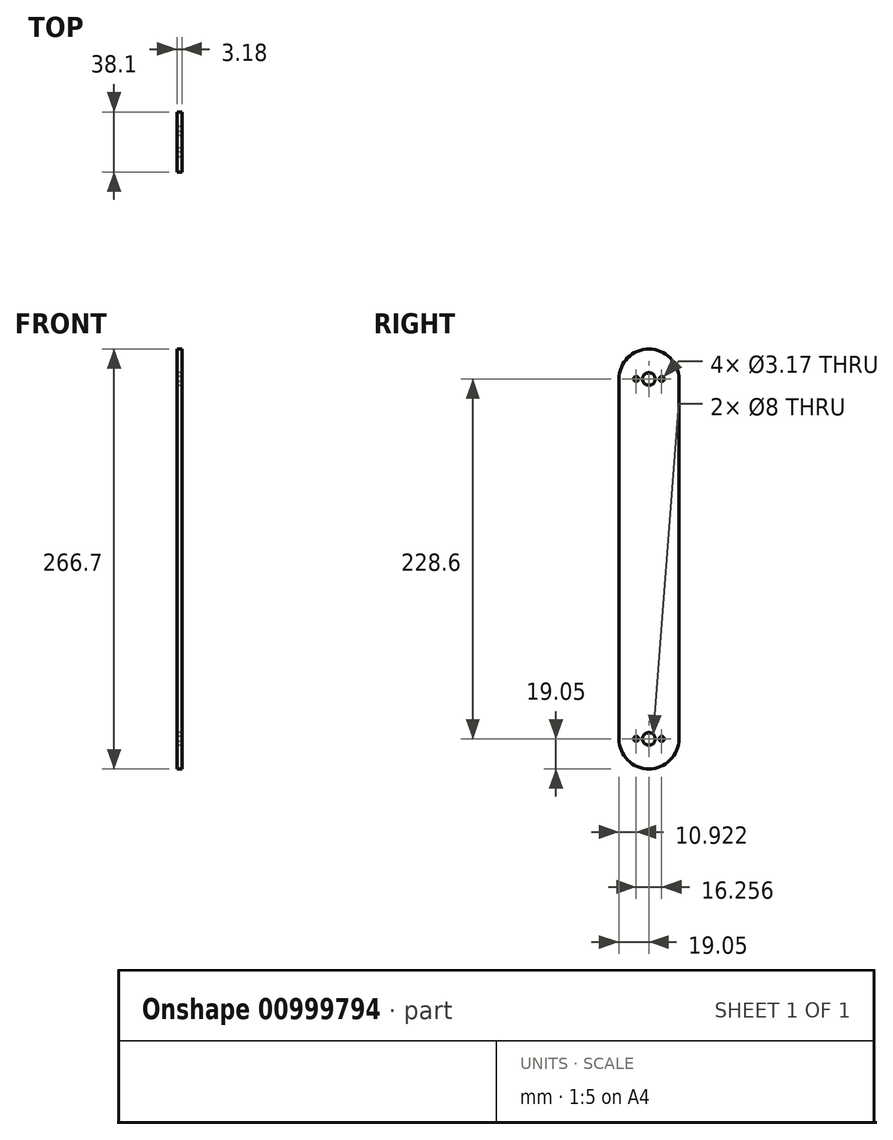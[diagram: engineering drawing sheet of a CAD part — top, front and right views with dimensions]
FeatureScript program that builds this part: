
annotation { "Feature Type Name" : "Feature", "Feature Type Description" : "" }
export const myFeature = defineFeature(function(context is Context, id is Id, definition is map)
    precondition{}
    {
        {
            var Q0;
            Q0=qCreatedBy(makeId("Right.planeOp"),FACE);
            var sketch = newSketch(context, id + "F0", { "sketchPlane" : qUnion([Q0])});
            skLineSegment(sketch, "E0.left", {"start": v(-19.05, 114.3) * mm, "end": v(-19.05, -114.3) * mm});
            skLineSegment(sketch, "E0.right", {"start": v(19.05, 114.3) * mm, "end": v(19.05, -114.3) * mm});
            skPoint(sketch, "E0.middle", {"position": v(0, 0) * mm});
            skArc(sketch, "E1", {"start": v(-19.05, -114.3) * mm, "mid": v(0, -133.35) * mm, "end": v(19.05, -114.3) * mm});
            skArc(sketch, "E2", {"start": v(19.05, 114.3) * mm, "mid": v(0, 133.35) * mm, "end": v(-19.05, 114.3) * mm});
            skCircle(sketch, "E3", {"center": v(0, 114.3) * mm, "radius": 4 * mm});
            skCircle(sketch, "E4", {"center": v(0, -114.3) * mm, "radius": 4 * mm});
            skCircle(sketch, "E5", {"center": v(8.13, 114.3) * mm, "radius": 1.59 * mm});
            skCircle(sketch, "E6", {"center": v(-8.13, 114.3) * mm, "radius": 1.59 * mm});
            skCircle(sketch, "E7", {"center": v(-8.13, -114.3) * mm, "radius": 1.59 * mm});
            skCircle(sketch, "E8", {"center": v(8.13, -114.3) * mm, "radius": 1.59 * mm});
            skLineSegment(sketch, "E9", {"start": v(0, 133.35) * mm, "end": v(0, 114.3) * mm});
            skSolve(sketch);
        }
        {
            var Q0;
            Q0=makeQuery(id+"F0.imprint","IMPRINT",FACE,{"disambiguationData":[TD([[makeQuery(id+"F0.imprint","IMPRINT",EDGE,{"derivedFrom":sQuery(id+"F0.wireOp",EDGE,"E0.left")}),1.0]])]});
            extrude(context, id + "F1", {"entities" : qUnion([Q0]), "depth" : 3.17 * mm, "offsetDistance" : 25.4 * mm, "symmetric" : true});
        }
    });
